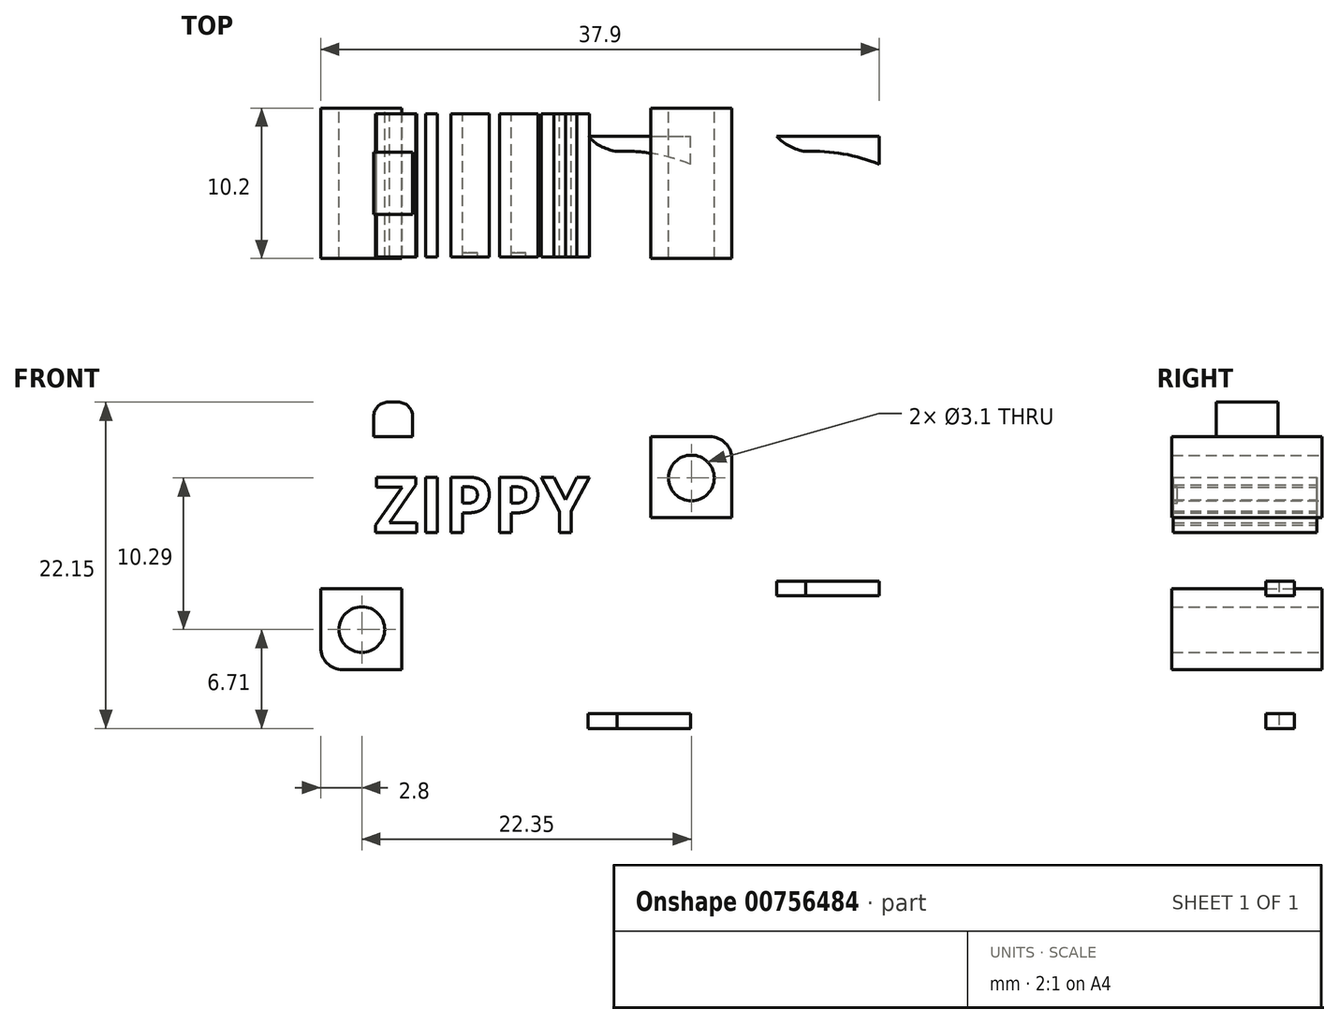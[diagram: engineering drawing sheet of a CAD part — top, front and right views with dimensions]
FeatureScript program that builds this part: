
annotation { "Feature Type Name" : "Feature", "Feature Type Description" : "" }
export const myFeature = defineFeature(function(context is Context, id is Id, definition is map)
    precondition{}
    {
        {
            var Q0;
            Q0=qCreatedBy(makeId("Front.planeOp"),FACE);
            var sketch = newSketch(context, id + "F0", { "sketchPlane" : qUnion([Q0])});
            skLineSegment(sketch, "E0.bottom", {"start": v(-10.95, 7.9) * mm, "end": v(12.45, 7.9) * mm});
            skLineSegment(sketch, "E0.top", {"start": v(-12.45, -7.9) * mm, "end": v(10.95, -7.9) * mm});
            skLineSegment(sketch, "E0.left", {"start": v(-13.95, 4.9) * mm, "end": v(-13.95, -6.4) * mm});
            skLineSegment(sketch, "E0.right", {"start": v(13.95, 6.4) * mm, "end": v(13.95, -4.9) * mm});
            skPoint(sketch, "E0.middle", {"position": v(0, 0) * mm});
            skCircle(sketch, "E1", {"center": v(11.2, 5.1) * mm, "radius": 1.55 * mm});
            skCircle(sketch, "E2", {"center": v(-11.15, -5.2) * mm, "radius": 1.55 * mm});
            skPoint(sketch, "E3.visualSharp", {"position": v(-13.95, 7.9) * mm});
            skArc(sketch, "E3.filletArc", {"start": v(-10.95, 7.9) * mm, "mid": v(-13.07, 7.02) * mm, "end": v(-13.95, 4.9) * mm});
            skPoint(sketch, "E4.visualSharp", {"position": v(13.95, -7.9) * mm});
            skArc(sketch, "E4.filletArc", {"start": v(10.95, -7.9) * mm, "mid": v(13.07, -7.02) * mm, "end": v(13.95, -4.9) * mm});
            skPoint(sketch, "E5.visualSharp", {"position": v(13.95, 7.9) * mm});
            skArc(sketch, "E5.filletArc", {"start": v(13.95, 6.4) * mm, "mid": v(13.51, 7.46) * mm, "end": v(12.45, 7.9) * mm});
            skPoint(sketch, "E6.visualSharp", {"position": v(-13.95, -7.9) * mm});
            skArc(sketch, "E6.filletArc", {"start": v(-13.95, -6.4) * mm, "mid": v(-13.51, -7.46) * mm, "end": v(-12.45, -7.9) * mm});
            skLineSegment(sketch, "E7.bottom", {"start": v(-10.35, 10.25) * mm, "end": v(-7.7, 10.25) * mm});
            skLineSegment(sketch, "E7.top", {"start": v(-10.35, 7.9) * mm, "end": v(-7.7, 7.9) * mm});
            skLineSegment(sketch, "E7.left", {"start": v(-10.35, 10.25) * mm, "end": v(-10.35, 7.9) * mm});
            skLineSegment(sketch, "E7.right", {"start": v(-7.7, 10.25) * mm, "end": v(-7.7, 7.9) * mm});
            skLineSegment(sketch, "E8.bottom", {"start": v(1.15, -7.9) * mm, "end": v(2.15, -7.9) * mm});
            skLineSegment(sketch, "E8.top", {"start": v(1.15, -10.9) * mm, "end": v(2.15, -10.9) * mm});
            skLineSegment(sketch, "E8.left", {"start": v(1.15, -7.9) * mm, "end": v(1.15, -10.9) * mm});
            skLineSegment(sketch, "E8.right", {"start": v(2.15, -7.9) * mm, "end": v(2.15, -10.9) * mm});
            skLineSegment(sketch, "E9.bottom", {"start": v(1.15, -10.9) * mm, "end": v(11.15, -10.9) * mm});
            skLineSegment(sketch, "E9.top", {"start": v(1.15, -11.9) * mm, "end": v(11.15, -11.9) * mm});
            skLineSegment(sketch, "E9.left", {"start": v(1.15, -10.9) * mm, "end": v(1.15, -11.9) * mm});
            skLineSegment(sketch, "E9.right", {"start": v(11.15, -10.9) * mm, "end": v(11.15, -11.9) * mm});
            skLineSegment(sketch, "E10.bottom", {"start": v(13.95, -1.9) * mm, "end": v(23.95, -1.9) * mm});
            skLineSegment(sketch, "E10.top", {"start": v(13.95, -2.9) * mm, "end": v(23.95, -2.9) * mm});
            skLineSegment(sketch, "E10.left", {"start": v(13.95, -1.9) * mm, "end": v(13.95, -2.9) * mm});
            skLineSegment(sketch, "E10.right", {"start": v(23.95, -1.9) * mm, "end": v(23.95, -2.9) * mm});
            skLineSegment(sketch, "E11", {"start": v(-13.95, -2.4) * mm, "end": v(-8.45, -2.4) * mm});
            skLineSegment(sketch, "E12", {"start": v(-8.45, -2.4) * mm, "end": v(-8.45, -7.9) * mm});
            skLineSegment(sketch, "E13", {"start": v(13.95, 2.4) * mm, "end": v(8.45, 2.4) * mm});
            skLineSegment(sketch, "E14", {"start": v(8.45, 2.4) * mm, "end": v(8.45, 7.9) * mm});
            skText(sketch, "E15", { "text": "ZIPPY", "fontName": "OpenSans-Bold.ttf"});
            const initialGuessF0  = {"E15": [-0.01035, 0.0014, 1, 0, 0.00378]};
            skSetInitialGuess(sketch, initialGuessF0);
            skSolve(sketch);
        }
        {
            var Q0;
            {var subQ2=sQuery(id+"F0.wireOp",EDGE,"E3.filletArc");Q0=makeQuery(id+"F0.imprint","IMPRINT",FACE,{"disambiguationData":[TD([[makeQuery(id+"F0.imprint","IMPRINT",EDGE,{"derivedFrom":subQ2}),1.0]])]});}
            var Q1;
            Q1=makeQuery(id+"F0.imprint","IMPRINT",FACE,{"disambiguationData":[TD([[makeQuery(id+"F0.imprint","IMPRINT",EDGE,{"derivedFrom":sQuery(id+"F0.wireOp",EDGE,"E15.sketch_text.stroke-30")}),1.0]])]});
            var Q2;
            Q2=makeQuery(id+"F0.imprint","IMPRINT",FACE,{"disambiguationData":[TD([[makeQuery(id+"F0.imprint","IMPRINT",EDGE,{"derivedFrom":sQuery(id+"F0.wireOp",EDGE,"E15.sketch_text.stroke-14")}),1.0]])]});
            var Q3;
            Q3=makeQuery(id+"F0.imprint","IMPRINT",FACE,{"disambiguationData":[TD([[makeQuery(id+"F0.imprint","IMPRINT",EDGE,{"derivedFrom":sQuery(id+"F0.wireOp",EDGE,"E15.sketch_text.stroke-14")}),-1.0]])]});
            var Q4;
            Q4=makeQuery(id+"F0.imprint","IMPRINT",FACE,{"disambiguationData":[TD([[makeQuery(id+"F0.imprint","IMPRINT",EDGE,{"derivedFrom":sQuery(id+"F0.wireOp",EDGE,"E15.sketch_text.stroke-10")}),-1.0]])]});
            var Q5;
            Q5=makeQuery(id+"F0.imprint","IMPRINT",FACE,{"disambiguationData":[TD([[makeQuery(id+"F0.imprint","IMPRINT",EDGE,{"derivedFrom":sQuery(id+"F0.wireOp",EDGE,"E15.sketch_text.stroke-0")}),-1.0]])]});
            var Q6;
            Q6=makeQuery(id+"F0.imprint","IMPRINT",FACE,{"disambiguationData":[TD([[makeQuery(id+"F0.imprint","IMPRINT",EDGE,{"derivedFrom":sQuery(id+"F0.wireOp",EDGE,"E15.sketch_text.stroke-30")}),-1.0]])]});
            var Q7;
            Q7=makeQuery(id+"F0.imprint","IMPRINT",FACE,{"disambiguationData":[TD([[makeQuery(id+"F0.imprint","IMPRINT",EDGE,{"derivedFrom":sQuery(id+"F0.wireOp",EDGE,"E15.sketch_text.stroke-46")}),-1.0]])]});
            extrude(context, id + "F1", {"entities" : qUnion([Q0, Q1, Q2, Q3, Q4, Q5, Q6, Q7]), "depth" : 9.45 * mm, "offsetDistance" : 25 * mm, "symmetric" : true});
        }
        {
            var Q0;
            Q0=makeQuery(id+"F0.imprint","IMPRINT",FACE,{"disambiguationData":[TD([[makeQuery(id+"F0.imprint","IMPRINT",EDGE,{"derivedFrom":sQuery(id+"F0.wireOp",EDGE,"E1")}),-1.0]])]});
            var Q1;
            Q1=makeQuery(id+"F0.imprint","IMPRINT",FACE,{"disambiguationData":[TD([[makeQuery(id+"F0.imprint","IMPRINT",EDGE,{"derivedFrom":sQuery(id+"F0.wireOp",EDGE,"E2")}),-1.0]])]});
            extrude(context, id + "F2", {"entities" : qUnion([Q0, Q1]), "operationType" : NewBodyOperationType.ADD, "depth" : 10.2 * mm, "offsetDistance" : 25 * mm, "symmetric" : true});
        }
        {
            var Q0;
            Q0=makeQuery(id+"F0.imprint","IMPRINT",FACE,{"disambiguationData":[TD([[makeQuery(id+"F0.imprint","IMPRINT",EDGE,{"derivedFrom":sQuery(id+"F0.wireOp",EDGE,"E7.bottom")}),-1.0]])]});
            extrude(context, id + "F3", {"entities" : qUnion([Q0]), "operationType" : NewBodyOperationType.ADD, "depth" : 4.2 * mm, "offsetDistance" : 25 * mm, "symmetric" : true});
        }
        {
            var Q0;
            Q0=makeQuery(id+"F0.imprint","IMPRINT",FACE,{"disambiguationData":[TD([[makeQuery(id+"F0.imprint","IMPRINT",EDGE,{"derivedFrom":sQuery(id+"F0.wireOp",EDGE,"E15.sketch_text.stroke-0")}),-1.0]])]});
            var Q1;
            Q1=makeQuery(id+"F0.imprint","IMPRINT",FACE,{"disambiguationData":[TD([[makeQuery(id+"F0.imprint","IMPRINT",EDGE,{"derivedFrom":sQuery(id+"F0.wireOp",EDGE,"E15.sketch_text.stroke-10")}),-1.0]])]});
            var Q2;
            Q2=makeQuery(id+"F0.imprint","IMPRINT",FACE,{"disambiguationData":[TD([[makeQuery(id+"F0.imprint","IMPRINT",EDGE,{"derivedFrom":sQuery(id+"F0.wireOp",EDGE,"E15.sketch_text.stroke-14")}),-1.0]])]});
            var Q3;
            Q3=makeQuery(id+"F0.imprint","IMPRINT",FACE,{"disambiguationData":[TD([[makeQuery(id+"F0.imprint","IMPRINT",EDGE,{"derivedFrom":sQuery(id+"F0.wireOp",EDGE,"E15.sketch_text.stroke-30")}),-1.0]])]});
            var Q4;
            Q4=makeQuery(id+"F0.imprint","IMPRINT",FACE,{"disambiguationData":[TD([[makeQuery(id+"F0.imprint","IMPRINT",EDGE,{"derivedFrom":sQuery(id+"F0.wireOp",EDGE,"E15.sketch_text.stroke-46")}),-1.0]])]});
            extrude(context, id + "F4", {"entities" : qUnion([Q0, Q1, Q2, Q3, Q4]), "operationType" : NewBodyOperationType.ADD, "depth" : 5 * mm, "offsetDistance" : 25 * mm});
        }
        {
            var Q0;
            Q0=makeQuery(id+"F0.imprint","IMPRINT",FACE,{"disambiguationData":[TD([[makeQuery(id+"F0.imprint","IMPRINT",EDGE,{"derivedFrom":sQuery(id+"F0.wireOp",EDGE,"E10.bottom")}),-1.0]])]});
            var Q1;
            Q1=makeQuery(id+"F0.imprint","IMPRINT",FACE,{"disambiguationData":[TD([[makeQuery(id+"F0.imprint","IMPRINT",EDGE,{"derivedFrom":sQuery(id+"F0.wireOp",EDGE,"E9.top")}),1.0]])]});
            var Q2;
            Q2=makeQuery(id+"F0.imprint","IMPRINT",FACE,{"disambiguationData":[TD([[makeQuery(id+"F0.imprint","IMPRINT",EDGE,{"derivedFrom":sQuery(id+"F0.wireOp",EDGE,"E8.bottom")}),-1.0]])]});
            extrude(context, id + "F5", {"entities" : qUnion([Q0, Q1, Q2]), "operationType" : NewBodyOperationType.ADD, "depth" : 6.4 * mm, "offsetDistance" : 25 * mm, "symmetric" : true});
        }
        {
            var Q0;
            Q0=makeQuery(id+"F5.opExtrude","SWEPT_FACE",FACE,{"disambiguationData":[OSD([sQuery(id+"F0.wireOp",EDGE,"E9.top")])]});
            var sketch = newSketch(context, id + "F6", { "sketchPlane" : qUnion([Q0])});
            skLineSegment(sketch, "E16.0", {"start": v(1.15, 3.2) * mm, "end": v(1.15, -3.2) * mm});
            skLineSegment(sketch, "E16.1", {"start": v(1.15, 3.2) * mm, "end": v(11.15, 3.2) * mm});
            skLineSegment(sketch, "E16.2", {"start": v(1.15, -3.2) * mm, "end": v(11.15, -3.2) * mm});
            skLineSegment(sketch, "E16.3", {"start": v(11.15, 3.2) * mm, "end": v(11.15, -3.2) * mm});
            skLineSegment(sketch, "E17", {"start": v(1.15, 0) * mm, "end": v(11.15, 0) * mm, "construction": true});
            skArc(sketch, "E18", {"start": v(4.18, 3.2) * mm, "mid": v(5.07, 2.51) * mm, "end": v(6.15, 2.16) * mm});
            skPoint(sketch, "E18.endSnap0", {"position": v(6.15, 3.2) * mm});
            skArc(sketch, "E19", {"start": v(11.15, 1.28) * mm, "mid": v(8.7, 2) * mm, "end": v(6.15, 2.16) * mm});
            skArc(sketch, "E20.MirrorCS", {"start": v(4.18, -3.2) * mm, "mid": v(5.07, -2.51) * mm, "end": v(6.15, -2.16) * mm});
            skArc(sketch, "E21.MirrorCS", {"start": v(11.15, -1.28) * mm, "mid": v(8.7, -2) * mm, "end": v(6.15, -2.16) * mm});
            skCircle(sketch, "E22", {"center": v(9.01, 0) * mm, "radius": 0.9 * mm});
            skSolve(sketch);
        }
        {
            var Q0;
            {var subQ3=sQuery(id+"F6.wireOp",EDGE,"E18");Q0=makeQuery(id+"F6.imprint","IMPRINT",FACE,{"disambiguationData":[TD([[makeQuery(id+"F6.imprint","IMPRINT",EDGE,{"derivedFrom":subQ3}),1.0]])]});}
            var Q1;
            {var subQ3=sQuery(id+"F6.wireOp",EDGE,"E20.MirrorCS");Q1=makeQuery(id+"F6.imprint","IMPRINT",FACE,{"disambiguationData":[TD([[makeQuery(id+"F6.imprint","IMPRINT",EDGE,{"derivedFrom":subQ3}),-1.0]])]});}
            var Q2;
            Q2=makeQuery(id+"F6.imprint","IMPRINT",FACE,{"disambiguationData":[TD([[makeQuery(id+"F6.imprint","IMPRINT",EDGE,{"derivedFrom":sQuery(id+"F6.wireOp",EDGE,"E22")}),1.0]])]});
            extrude(context, id + "F7", {"entities" : qUnion([Q0, Q1, Q2]), "operationType" : NewBodyOperationType.REMOVE, "endBound" : BoundingType.UP_TO_NEXT, "oppositeDirection" : true, "depth" : 25 * mm, "offsetDistance" : 25 * mm});
        }
        {
            var Q0;
            Q0=makeQuery(id+"F5.opExtrude","SWEPT_FACE",FACE,{"disambiguationData":[OSD([sQuery(id+"F0.wireOp",EDGE,"E10.top")])]});
            var sketch = newSketch(context, id + "F8", { "sketchPlane" : qUnion([Q0])});
            skLineSegment(sketch, "E23.0", {"start": v(13.95, 3.2) * mm, "end": v(13.95, -3.2) * mm});
            skLineSegment(sketch, "E23.1", {"start": v(13.95, 3.2) * mm, "end": v(23.95, 3.2) * mm});
            skLineSegment(sketch, "E23.2", {"start": v(13.95, -3.2) * mm, "end": v(23.95, -3.2) * mm});
            skLineSegment(sketch, "E23.3", {"start": v(23.95, 3.2) * mm, "end": v(23.95, -3.2) * mm});
            skLineSegment(sketch, "E24", {"start": v(13.95, 0) * mm, "end": v(23.95, 0) * mm, "construction": true});
            skArc(sketch, "E25", {"start": v(16.98, 3.2) * mm, "mid": v(17.87, 2.51) * mm, "end": v(18.95, 2.16) * mm});
            skPoint(sketch, "E25.endSnap0", {"position": v(18.95, 3.2) * mm});
            skArc(sketch, "E26", {"start": v(23.95, 1.28) * mm, "mid": v(21.5, 2) * mm, "end": v(18.95, 2.16) * mm});
            skArc(sketch, "E27.MirrorCS", {"start": v(16.98, -3.2) * mm, "mid": v(17.87, -2.51) * mm, "end": v(18.95, -2.16) * mm});
            skArc(sketch, "E28.MirrorCS", {"start": v(23.95, -1.28) * mm, "mid": v(21.5, -2) * mm, "end": v(18.95, -2.16) * mm});
            skCircle(sketch, "E29", {"center": v(21.81, 0) * mm, "radius": 0.9 * mm});
            skSolve(sketch);
        }
        {
            var Q0;
            {var subQ3=sQuery(id+"F8.wireOp",EDGE,"E25");Q0=makeQuery(id+"F8.imprint","IMPRINT",FACE,{"disambiguationData":[TD([[makeQuery(id+"F8.imprint","IMPRINT",EDGE,{"derivedFrom":subQ3}),1.0]])]});}
            var Q1;
            {var subQ3=sQuery(id+"F8.wireOp",EDGE,"E27.MirrorCS");Q1=makeQuery(id+"F8.imprint","IMPRINT",FACE,{"disambiguationData":[TD([[makeQuery(id+"F8.imprint","IMPRINT",EDGE,{"derivedFrom":subQ3}),-1.0]])]});}
            var Q2;
            Q2=makeQuery(id+"F8.imprint","IMPRINT",FACE,{"disambiguationData":[TD([[makeQuery(id+"F8.imprint","IMPRINT",EDGE,{"derivedFrom":sQuery(id+"F8.wireOp",EDGE,"E29")}),1.0]])]});
            extrude(context, id + "F9", {"entities" : qUnion([Q0, Q1, Q2]), "operationType" : NewBodyOperationType.REMOVE, "endBound" : BoundingType.UP_TO_NEXT, "oppositeDirection" : true, "depth" : 25 * mm, "offsetDistance" : 25 * mm});
        }
        {
            var Q0;
            Q0=makeQuery(id+"F3.opExtrude","SWEPT_EDGE",EDGE,{"disambiguationData":[OSD([sQuery(id+"F0.wireOp",EDGE,"E7.bottom"),sQuery(id+"F0.wireOp",EDGE,"E7.left")])]});
            var Q1;
            Q1=makeQuery(id+"F3.opExtrude","SWEPT_EDGE",EDGE,{"disambiguationData":[OSD([sQuery(id+"F0.wireOp",EDGE,"E7.bottom"),sQuery(id+"F0.wireOp",EDGE,"E7.right")])]});
            fillet(context, id + "F10", {"entities" : qUnion([Q0, Q1]), "radius" : 1 * mm, "tangentPropagation" : true, "allowEdgeOverflow" : false});
        }
    });
